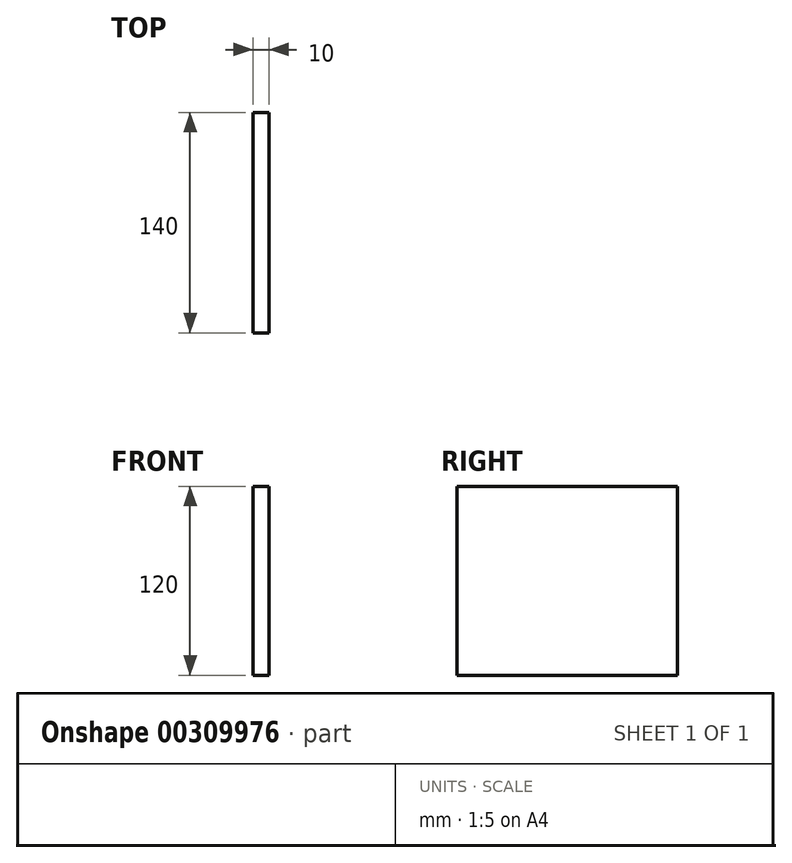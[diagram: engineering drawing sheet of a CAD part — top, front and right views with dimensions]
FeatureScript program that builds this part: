
annotation { "Feature Type Name" : "Feature", "Feature Type Description" : "" }
export const myFeature = defineFeature(function(context is Context, id is Id, definition is map)
    precondition{}
    {
        {
            var Q0;
            Q0=qCreatedBy(makeId("Front.planeOp"),FACE);
            var sketch = newSketch(context, id + "F0", { "sketchPlane" : qUnion([Q0])});
            skLineSegment(sketch, "E0.bottom", {"start": v(-14.46, 123.97) * mm, "end": v(-4.46, 123.97) * mm});
            skLineSegment(sketch, "E0.top", {"start": v(-14.46, 3.97) * mm, "end": v(-4.46, 3.97) * mm});
            skLineSegment(sketch, "E0.left", {"start": v(-14.46, 123.97) * mm, "end": v(-14.46, 3.97) * mm});
            skLineSegment(sketch, "E0.right", {"start": v(-4.46, 123.97) * mm, "end": v(-4.46, 3.97) * mm});
            skSolve(sketch);
        }
        {
            var Q0;
            Q0 = qSketchRegion(id + "F0", true);
            extrude(context, id + "F1", {"entities" : qUnion([Q0]), "depth" : 140 * mm});
        }
    });
